FCSTD DOCUMENT  (FreeCAD 0.19R16830 +1496 (Git))
Label: asm_V4
License: All rights reserved
LicenseURL: http://en.wikipedia.org/wiki/All_rights_reserved
objects: PartDesign::CoordinateSystem×18, App::Link×13, App::FeaturePython×13, Sketcher::SketchObject×5, PartDesign::Point×4, App::DocumentObjectGroup×1, App::Part×1
note: 27 computed .brp shape members not serialized (recipe doc carries the construction recipe); baked Part::Feature solids carry a one-line shape summary decoded from their .brp
EXTERNAL_REF file=Crankshaft.FCStd obj=Model
EXTERNAL_REF file=Cylindre.FCStd obj=Part
EXTERNAL_REF file=Piston.FCStd obj=Part
EXTERNAL_REF file=asm_Bielle.fcstd obj=Model

FEATURE [PartDesign::CoordinateSystem] LCS_0
  AttacherType = Attacher::AttachEngine3D
FEATURE [PartDesign::CoordinateSystem] LCS_crankshaft
  AttacherType = Attacher::AttachEngine3D
  AttachmentOffset = pos=(0,0,0) rot=(0,1,0;12.5664rad)
  MapMode = 2
  Support = -> [LCS_0]
FEATURE [App::Link] Crankshaft
  LinkedObject = -> <external Crankshaft.FCStd>#Model
  expr: Placement = <<LCS_crankshaft>>.Placement.multiply(<<constr_Crankshaft>>.AttachmentOffset).multiply(.<<LCS_0.>>.Placement.inverse())
FEATURE [App::FeaturePython] constr_Crankshaft  # WARN: FeaturePython — macro-defined, semantics opaque (R4)
  AttachedTo = Parent Assembly
  AttachmentLCS = LCS_crankshaft
  ConstraintType = AttachmentByLCS
  LinkName = Crankshaft
  LinkedFile = Crankshaft
  LinkedPartLCS = LCS_0
FEATURE [PartDesign::Point] Point_clocking1
  AttacherType = Attacher::AttachEnginePoint
  Placement = pos=(-28.2843,6.3e-15,28.2843) rot=(0,1,0;0.785398rad)
  expr: Placement = <<Crankshaft>>.Placement.multiply(<<Crankshaft>>.<<LCS_clocking1.>>.Placement)
FEATURE [PartDesign::Point] Point_clocking2
  AttacherType = Attacher::AttachEnginePoint
  Placement = pos=(28.2843,6.3e-15,28.2843) rot=(0.382683,0,-0.92388;3.14159rad)
  expr: Placement = <<Crankshaft>>.Placement.multiply(<<Crankshaft>>.<<LCS_clocking2.>>.Placement)
FEATURE [PartDesign::Point] Point_clocking3
  AttacherType = Attacher::AttachEnginePoint
  Placement = pos=(28.2843,-6.3e-15,-28.2843) rot=(-0.382683,0,-0.92388;3.14159rad)
  expr: Placement = <<Crankshaft>>.Placement.multiply(<<Crankshaft>>.<<LCS_clocking3.>>.Placement)
FEATURE [PartDesign::Point] Point_clocking4
  AttacherType = Attacher::AttachEnginePoint
  Placement = pos=(-28.2843,-6.3e-15,-28.2843) rot=(0,-1,0;0.785398rad)
  expr: Placement = <<Crankshaft>>.Placement.multiply(<<Crankshaft>>.<<LCS_clocking4.>>.Placement)
FEATURE [PartDesign::CoordinateSystem] LCS_cylindre1
  AttacherType = Attacher::AttachEngine3D
  Placement = pos=(0,50,0) rot=(0,0,1;0rad)
  expr: Placement = <<Crankshaft>>.Placement.multiply(<<Crankshaft>>.<<LCS_cylindre1.>>.Placement)
FEATURE [PartDesign::CoordinateSystem] LCS_cylindre2
  AttacherType = Attacher::AttachEngine3D
  Placement = pos=(0,100,0) rot=(0,0,1;0rad)
  expr: Placement = <<Crankshaft>>.Placement.multiply(<<Crankshaft>>.<<LCS_cylindre2.>>.Placement)
FEATURE [PartDesign::CoordinateSystem] LCS_cylindre3
  AttacherType = Attacher::AttachEngine3D
  Placement = pos=(0,160,0) rot=(0,0,1;0rad)
  expr: Placement = <<Crankshaft>>.Placement.multiply(<<Crankshaft>>.<<LCS_cylindre3.>>.Placement)
FEATURE [PartDesign::CoordinateSystem] LCS_cylindre4
  AttacherType = Attacher::AttachEngine3D
  Placement = pos=(0,210,0) rot=(0,0,1;0rad)
  expr: Placement = <<Crankshaft>>.Placement.multiply(<<Crankshaft>>.<<LCS_cylindre4.>>.Placement)
FEATURE [Sketcher::SketchObject] Sketch_V
  MapMode = 3
  Placement = pos=(0,0,0) rot=(1,0,0;1.5708rad)
  Support = -> [LCS_0]
  sketch-geometry (2):
    g0: LineSegment StartX=0 StartY=0 StartZ=0 EndX=169.706 EndY=169.706 EndZ=0
    g1: LineSegment StartX=0 StartY=0 StartZ=0 EndX=-169.706 EndY=169.706 EndZ=0
  constraints (5):
    c: Coincident(g0,g-1)
    c: Coincident(g1,g0)
    c: Symmetric(g1,g0,g-2)
    c: Angle(g0,g1) = 1.5708
    c: Distance(g1) = 240
FEATURE [Sketcher::SketchObject] Sketch_piston1
  ExternalGeometry = -> [Sketch_V,Point_clocking1]
  MapMode = 3
  Placement = pos=(0,50,0) rot=(1,0,0;1.5708rad)
  Support = -> [LCS_cylindre1]
  sketch-geometry (4):
    g0: LineSegment StartX=0 StartY=0 StartZ=0 EndX=-28.2843 EndY=28.2843 EndZ=0
    g1: LineSegment StartX=-28.2843 StartY=28.2843 StartZ=0 EndX=-134.35 EndY=134.35 EndZ=0
    g2: LineSegment StartX=-134.35 StartY=134.35 StartZ=0 EndX=-162.635 EndY=162.635 EndZ=0
    g3: LineSegment StartX=-169.706 StartY=169.706 StartZ=0 EndX=-162.635 EndY=162.635 EndZ=0
  constraints (11):
    c: Coincident(g0,g-1)
    c: Coincident(g0,g-4)
    c: Coincident(g1,g0)
    c: PointOnObject(g1,g-3)
    c: Coincident(g2,g1)
    c: PointOnObject(g2,g-3)
    c: Parallel(g3,g-3)
    c: Coincident(g-3,g3)
    c: Distance(g3) = 10
    c: Distance(g3,g2) = 10
    c: Distance(g1) = 150
FEATURE [Sketcher::SketchObject] Sketch_piston2
  ExternalGeometry = -> [Point_clocking2,Sketch_V]
  MapMode = 3
  Placement = pos=(0,100,0) rot=(1,0,0;1.5708rad)
  Support = -> [LCS_cylindre2]
  sketch-geometry (4):
    g0: LineSegment StartX=0 StartY=0 StartZ=0 EndX=28.2843 EndY=28.2843 EndZ=0
    g1: LineSegment StartX=28.2843 StartY=28.2843 StartZ=0 EndX=134.35 EndY=134.35 EndZ=0
    g2: LineSegment StartX=134.35 StartY=134.35 StartZ=0 EndX=162.635 EndY=162.635 EndZ=0
    g3: LineSegment StartX=169.706 StartY=169.706 StartZ=0 EndX=162.635 EndY=162.635 EndZ=0
  constraints (11):
    c: Coincident(g0,g-3)
    c: Coincident(g-1,g0)
    c: Coincident(g1,g0)
    c: PointOnObject(g1,g-4)
    c: Coincident(g2,g1)
    c: PointOnObject(g2,g-4)
    c: Parallel(g3,g-4)
    c: Coincident(g3,g-4)
    c: Distance(g3) = 10
    c: Distance(g3,g2) = 10
    c: Distance(g1) = 150
FEATURE [Sketcher::SketchObject] Sketch_piston3
  ExternalGeometry = -> [Sketch_V,Point_clocking3]
  MapMode = 3
  Placement = pos=(0,160,0) rot=(1,0,0;1.5708rad)
  Support = -> [LCS_cylindre3]
  sketch-geometry (4):
    g0: LineSegment StartX=28.2843 StartY=-28.2843 StartZ=0 EndX=-1.78e-14 EndY=3.6e-15 EndZ=0
    g1: LineSegment StartX=28.2843 StartY=-28.2843 StartZ=0 EndX=-77.7817 EndY=77.7817 EndZ=0
    g2: LineSegment StartX=-169.706 StartY=169.706 StartZ=0 EndX=-162.635 EndY=162.635 EndZ=0
    g3: LineSegment StartX=-77.7817 StartY=77.7817 StartZ=0 EndX=-162.635 EndY=162.635 EndZ=0
  constraints (11):
    c: Coincident(g0,g-4)
    c: Coincident(g-1,g0)
    c: Coincident(g1,g0)
    c: PointOnObject(g1,g-3)
    c: Coincident(g2,g-3)
    c: Parallel(g2,g-3)
    c: Coincident(g3,g1)
    c: PointOnObject(g3,g-3)
    c: Distance(g2) = 10
    c: Distance(g2,g3) = 10
    c: Distance(g1) = 150
FEATURE [Sketcher::SketchObject] Sketch_piston4
  ExternalGeometry = -> [Sketch_V,Point_clocking4]
  MapMode = 3
  Placement = pos=(0,210,0) rot=(1,0,0;1.5708rad)
  Support = -> [LCS_cylindre4]
  sketch-geometry (4):
    g0: LineSegment StartX=-28.2843 StartY=-28.2843 StartZ=0 EndX=77.7817 EndY=77.7817 EndZ=0
    g1: LineSegment StartX=-28.2843 StartY=-28.2843 StartZ=0 EndX=-3.6e-15 EndY=-2.49e-14 EndZ=0
    g2: LineSegment StartX=77.7817 StartY=77.7817 StartZ=0 EndX=162.635 EndY=162.635 EndZ=0
    g3: LineSegment StartX=169.706 StartY=169.706 StartZ=0 EndX=162.635 EndY=162.635 EndZ=0
  constraints (11):
    c: Coincident(g0,g-4)
    c: PointOnObject(g0,g-3)
    c: Coincident(g1,g0)
    c: Coincident(g1,g-1)
    c: Coincident(g2,g0)
    c: PointOnObject(g2,g-3)
    c: Coincident(g3,g-3)
    c: Parallel(g3,g-3)
    c: Distance(g3) = 10
    c: Distance(g2,g3) = 10
    c: Distance(g0) = 150
FEATURE [PartDesign::CoordinateSystem] LCS_cylindre1001
  AttacherType = Attacher::AttachEngine3D
  MapMode = 50
  Placement = pos=(-169.706,50,169.706) rot=(0,1,0;0.785398rad)
  Support = -> [Sketch_piston1]
FEATURE [PartDesign::CoordinateSystem] LCS_cylindre2001
  AttacherType = Attacher::AttachEngine3D
  MapMode = 49
  Placement = pos=(169.706,100,169.706) rot=(-0.382683,0,0.92388;3.14159rad)
  Support = -> [Sketch_piston2]
FEATURE [PartDesign::CoordinateSystem] LCS_cylindre3001
  AttacherType = Attacher::AttachEngine3D
  MapMode = 49
  Placement = pos=(-169.706,160,169.706) rot=(0,1,0;0.785398rad)
  Support = -> [Sketch_piston3]
FEATURE [PartDesign::CoordinateSystem] LCS_cylindre4001
  AttacherType = Attacher::AttachEngine3D
  MapMode = 49
  Placement = pos=(169.706,210,169.706) rot=(-0.382683,0,0.92388;3.14159rad)
  Support = -> [Sketch_piston4]
FEATURE [App::Link] Cylindre_1
  LinkPlacement = pos=(-169.706,50,169.706) rot=(0,1,0;2.35619rad)
  LinkedObject = -> <external Cylindre.FCStd>#Part
  Placement = pos=(-169.706,50,169.706) rot=(0,1,0;2.35619rad)
  expr: Placement = <<LCS_cylindre1001>>.Placement.multiply(<<constr_Cylindre_1>>.AttachmentOffset).multiply(.<<LCS_0.>>.Placement.inverse())
FEATURE [App::FeaturePython] constr_Cylindre_1  # WARN: FeaturePython — macro-defined, semantics opaque (R4)
  AttachedTo = Parent Assembly
  AttachmentLCS = LCS_cylindre1001
  AttachmentOffset = pos=(0,0,0) rot=(0,1,0;1.5708rad)
  ConstraintType = AttachmentByLCS
  LinkName = Cylindre_1
  LinkedFile = Cylindre
  LinkedPartLCS = LCS_0
FEATURE [App::Link] Cylindre_2
  LinkPlacement = pos=(169.706,100,169.706) rot=(-0.92388,0,0.382683;3.14159rad)
  LinkedObject = -> <external Cylindre.FCStd>#Part
  Placement = pos=(169.706,100,169.706) rot=(-0.92388,0,0.382683;3.14159rad)
  expr: Placement = <<LCS_cylindre2001>>.Placement.multiply(<<constr_Cylindre_2>>.AttachmentOffset).multiply(.<<LCS_0.>>.Placement.inverse())
FEATURE [App::FeaturePython] constr_Cylindre_2  # WARN: FeaturePython — macro-defined, semantics opaque (R4)
  AttachedTo = Parent Assembly
  AttachmentLCS = LCS_cylindre2001
  AttachmentOffset = pos=(0,0,0) rot=(0,1,0;1.5708rad)
  ConstraintType = AttachmentByLCS
  LinkName = Cylindre_2
  LinkedFile = Cylindre
  LinkedPartLCS = LCS_0
FEATURE [App::Link] Cylindre_3
  LinkPlacement = pos=(-169.706,160,169.706) rot=(0,1,0;2.35619rad)
  LinkedObject = -> <external Cylindre.FCStd>#Part
  Placement = pos=(-169.706,160,169.706) rot=(0,1,0;2.35619rad)
  expr: Placement = <<LCS_cylindre3001>>.Placement.multiply(<<constr_Cylindre_3>>.AttachmentOffset).multiply(.<<LCS_0.>>.Placement.inverse())
FEATURE [App::FeaturePython] constr_Cylindre_3  # WARN: FeaturePython — macro-defined, semantics opaque (R4)
  AttachedTo = Parent Assembly
  AttachmentLCS = LCS_cylindre3001
  AttachmentOffset = pos=(0,0,0) rot=(0,1,0;1.5708rad)
  ConstraintType = AttachmentByLCS
  LinkName = Cylindre_3
  LinkedFile = Cylindre
  LinkedPartLCS = LCS_0
FEATURE [App::Link] Cylindre_4
  LinkPlacement = pos=(169.706,210,169.706) rot=(-0.92388,0,0.382683;3.14159rad)
  LinkedObject = -> <external Cylindre.FCStd>#Part
  Placement = pos=(169.706,210,169.706) rot=(-0.92388,0,0.382683;3.14159rad)
  expr: Placement = <<LCS_cylindre4001>>.Placement.multiply(<<constr_Cylindre_4>>.AttachmentOffset).multiply(.<<LCS_0.>>.Placement.inverse())
FEATURE [App::FeaturePython] constr_Cylindre_4  # WARN: FeaturePython — macro-defined, semantics opaque (R4)
  AttachedTo = Parent Assembly
  AttachmentLCS = LCS_cylindre4001
  AttachmentOffset = pos=(0,0,0) rot=(0,1,0;1.5708rad)
  ConstraintType = AttachmentByLCS
  LinkName = Cylindre_4
  LinkedFile = Cylindre
  LinkedPartLCS = LCS_0
FEATURE [PartDesign::CoordinateSystem] LCS_P1
  AttacherType = Attacher::AttachEngine3D
  MapMode = 49
  Placement = pos=(-134.35,50,134.35) rot=(0.382683,0,0.92388;3.14159rad)
  Support = -> [Sketch_piston1]
FEATURE [PartDesign::CoordinateSystem] LCS_B1
  AttacherType = Attacher::AttachEngine3D
  MapMode = 49
  Placement = pos=(-28.2843,50,28.2843) rot=(0.382683,0,0.92388;3.14159rad)
  Support = -> [Sketch_piston1]
FEATURE [PartDesign::CoordinateSystem] LCS_P2
  AttacherType = Attacher::AttachEngine3D
  MapMode = 49
  Placement = pos=(134.35,100,134.35) rot=(0,-1,0;0.785398rad)
  Support = -> [Sketch_piston2]
FEATURE [PartDesign::CoordinateSystem] LCS_B2
  AttacherType = Attacher::AttachEngine3D
  MapMode = 49
  Placement = pos=(28.2843,100,28.2843) rot=(0,-1,0;0.785398rad)
  Support = -> [Sketch_piston2]
FEATURE [PartDesign::CoordinateSystem] LCS_P3
  AttacherType = Attacher::AttachEngine3D
  MapMode = 49
  Placement = pos=(-77.7817,160,77.7817) rot=(0.382683,0,0.92388;3.14159rad)
  Support = -> [Sketch_piston3]
FEATURE [PartDesign::CoordinateSystem] LCS_B3
  AttacherType = Attacher::AttachEngine3D
  MapMode = 49
  Placement = pos=(28.2843,160,-28.2843) rot=(0.382683,0,0.92388;3.14159rad)
  Support = -> [Sketch_piston3]
FEATURE [PartDesign::CoordinateSystem] LCS_P4
  AttacherType = Attacher::AttachEngine3D
  MapMode = 49
  Placement = pos=(77.7817,210,77.7817) rot=(0,-1,0;0.785398rad)
  Support = -> [Sketch_piston4]
FEATURE [PartDesign::CoordinateSystem] LCS_B4
  AttacherType = Attacher::AttachEngine3D
  MapMode = 49
  Placement = pos=(-28.2843,210,-28.2843) rot=(0,-1,0;0.785398rad)
  Support = -> [Sketch_piston4]
FEATURE [App::Link] Piston_1
  LinkPlacement = pos=(-98.9949,50,98.9949) rot=(0,1,0;5.49779rad)
  LinkedObject = -> <external Piston.FCStd>#Part
  Placement = pos=(-98.9949,50,98.9949) rot=(0,1,0;5.49779rad)
  expr: Placement = <<LCS_P1>>.Placement.multiply(<<constr_Piston_1>>.AttachmentOffset).multiply(.<<LCS_axis.>>.Placement.inverse())
FEATURE [App::FeaturePython] constr_Piston_1  # WARN: FeaturePython — macro-defined, semantics opaque (R4)
  AttachedTo = Parent Assembly
  AttachmentLCS = LCS_P1
  AttachmentOffset = pos=(0,0,0) rot=(-0.57735,-0.57735,0.57735;4.18879rad)
  ConstraintType = AttachmentByLCS
  LinkName = Piston_1
  LinkedFile = Piston
  LinkedPartLCS = LCS_axis
FEATURE [App::Link] Piston_2
  LinkPlacement = pos=(98.9949,100,98.9949) rot=(-0.382683,0,-0.92388;3.14159rad)
  LinkedObject = -> <external Piston.FCStd>#Part
  Placement = pos=(98.9949,100,98.9949) rot=(-0.382683,0,-0.92388;3.14159rad)
  expr: Placement = <<LCS_P2>>.Placement.multiply(<<constr_Piston_2>>.AttachmentOffset).multiply(.<<LCS_axis.>>.Placement.inverse())
FEATURE [App::FeaturePython] constr_Piston_2  # WARN: FeaturePython — macro-defined, semantics opaque (R4)
  AttachedTo = Parent Assembly
  AttachmentLCS = LCS_P2
  AttachmentOffset = pos=(0,0,0) rot=(0.57735,0.57735,-0.57735;2.0944rad)
  ConstraintType = AttachmentByLCS
  LinkName = Piston_2
  LinkedFile = Piston
  LinkedPartLCS = LCS_axis
FEATURE [App::Link] Piston_3
  LinkPlacement = pos=(-42.4264,160,42.4264) rot=(0,1,0;5.49779rad)
  LinkedObject = -> <external Piston.FCStd>#Part
  Placement = pos=(-42.4264,160,42.4264) rot=(0,1,0;5.49779rad)
  expr: Placement = <<LCS_P3>>.Placement.multiply(<<constr_Piston_3>>.AttachmentOffset).multiply(.<<LCS_axis.>>.Placement.inverse())
FEATURE [App::FeaturePython] constr_Piston_3  # WARN: FeaturePython — macro-defined, semantics opaque (R4)
  AttachedTo = Parent Assembly
  AttachmentLCS = LCS_P3
  AttachmentOffset = pos=(0,0,0) rot=(-0.57735,-0.57735,0.57735;4.18879rad)
  ConstraintType = AttachmentByLCS
  LinkName = Piston_3
  LinkedFile = Piston
  LinkedPartLCS = LCS_axis
FEATURE [App::Link] Piston_4
  LinkPlacement = pos=(42.4264,210,42.4264) rot=(-0.382683,0,-0.92388;3.14159rad)
  LinkedObject = -> <external Piston.FCStd>#Part
  Placement = pos=(42.4264,210,42.4264) rot=(-0.382683,0,-0.92388;3.14159rad)
  expr: Placement = <<LCS_P4>>.Placement.multiply(<<constr_Piston_4>>.AttachmentOffset).multiply(.<<LCS_axis.>>.Placement.inverse())
FEATURE [App::FeaturePython] constr_Piston_4  # WARN: FeaturePython — macro-defined, semantics opaque (R4)
  AttachedTo = Parent Assembly
  AttachmentLCS = LCS_P4
  AttachmentOffset = pos=(0,0,0) rot=(0.57735,0.57735,-0.57735;2.0944rad)
  ConstraintType = AttachmentByLCS
  LinkName = Piston_4
  LinkedFile = Piston
  LinkedPartLCS = LCS_axis
FEATURE [App::Link] Bielle_1
  LinkPlacement = pos=(-116.673,50,116.673) rot=(-0.862856,0.357407,0.357407;1.71777rad)
  LinkedObject = -> <external asm_Bielle.fcstd>#Model
  Placement = pos=(-116.673,50,116.673) rot=(-0.862856,0.357407,0.357407;1.71777rad)
  expr: Placement = <<LCS_B1>>.Placement.multiply(<<constr_Bielle_1>>.AttachmentOffset).multiply(.<<LCS_Cuve.>>.Placement.inverse())
FEATURE [App::FeaturePython] constr_Bielle_1  # WARN: FeaturePython — macro-defined, semantics opaque (R4)
  AttachedTo = Parent Assembly
  AttachmentLCS = LCS_B1
  AttachmentOffset = pos=(0,0,0) rot=(0,0.707107,-0.707107;3.14159rad)
  ConstraintType = AttachmentByLCS
  LinkName = Bielle_1
  LinkedFile = asm_Bielle
  LinkedPartLCS = LCS_Cuve
FEATURE [App::Link] Bielle_2
  LinkPlacement = pos=(116.673,100,116.673) rot=(-0.281085,-0.678598,0.678598;3.68962rad)
  LinkedObject = -> <external asm_Bielle.fcstd>#Model
  Placement = pos=(116.673,100,116.673) rot=(-0.281085,-0.678598,0.678598;3.68962rad)
  expr: Placement = <<LCS_B2>>.Placement.multiply(<<constr_Bielle_2>>.AttachmentOffset).multiply(.<<LCS_Cuve.>>.Placement.inverse())
FEATURE [App::FeaturePython] constr_Bielle_2  # WARN: FeaturePython — macro-defined, semantics opaque (R4)
  AttachedTo = Parent Assembly
  AttachmentLCS = LCS_B2
  AttachmentOffset = pos=(0,0,0) rot=(0,-0.707107,0.707107;3.14159rad)
  ConstraintType = AttachmentByLCS
  LinkName = Bielle_2
  LinkedFile = asm_Bielle
  LinkedPartLCS = LCS_Cuve
FEATURE [App::Link] Bielle_3
  LinkPlacement = pos=(-60.1041,160,60.1041) rot=(0.862856,-0.357407,-0.357407;4.56541rad)
  LinkedObject = -> <external asm_Bielle.fcstd>#Model
  Placement = pos=(-60.1041,160,60.1041) rot=(0.862856,-0.357407,-0.357407;4.56541rad)
  expr: Placement = <<LCS_B3>>.Placement.multiply(<<constr_Bielle_3>>.AttachmentOffset).multiply(.<<LCS_Cuve.>>.Placement.inverse())
FEATURE [App::FeaturePython] constr_Bielle_3  # WARN: FeaturePython — macro-defined, semantics opaque (R4)
  AttachedTo = Parent Assembly
  AttachmentLCS = LCS_B3
  AttachmentOffset = pos=(0,0,0) rot=(0,-0.707107,0.707107;3.14159rad)
  ConstraintType = AttachmentByLCS
  LinkName = Bielle_3
  LinkedFile = asm_Bielle
  LinkedPartLCS = LCS_Cuve
FEATURE [App::Link] Bielle_4
  LinkPlacement = pos=(60.1041,210,60.1041) rot=(0.281085,0.678598,-0.678598;2.59356rad)
  LinkedObject = -> <external asm_Bielle.fcstd>#Model
  Placement = pos=(60.1041,210,60.1041) rot=(0.281085,0.678598,-0.678598;2.59356rad)
  expr: Placement = <<LCS_B4>>.Placement.multiply(<<constr_Bielle_4>>.AttachmentOffset).multiply(.<<LCS_Cuve.>>.Placement.inverse())
FEATURE [App::FeaturePython] constr_Bielle_4  # WARN: FeaturePython — macro-defined, semantics opaque (R4)
  AttachedTo = Parent Assembly
  AttachmentLCS = LCS_B4
  AttachmentOffset = pos=(0,0,0) rot=(0,0.707107,-0.707107;3.14159rad)
  ConstraintType = AttachmentByLCS
  LinkName = Bielle_4
  LinkedFile = asm_Bielle
  LinkedPartLCS = LCS_Cuve
FEATURE [App::DocumentObjectGroup] Constraints
  Group = -> [constr_Crankshaft,constr_Cylindre_1,constr_Cylindre_2,constr_Cylindre_3,constr_Cylindre_4,constr_Piston_1,constr_Piston_2,constr_Piston_3,constr_Piston_4,constr_Bielle_1,constr_Bielle_2,constr_Bielle_3,constr_Bielle_4]
FEATURE [App::Part] Model
  Group = -> [Constraints,LCS_0,LCS_crankshaft,Crankshaft,constr_Crankshaft,Point_clocking1,Point_clocking2,Point_clocking3,Point_clocking4,LCS_cylindre1,LCS_cylindre2,LCS_cylindre3,LCS_cylindre4,Sketch_V,Sketch_piston1,Sketch_piston2,Sketch_piston3,Sketch_piston4,LCS_cylindre1001,LCS_cylindre2001,LCS_cylindre3001,LCS_cylindre4001,Cylindre_1,constr_Cylindre_1,Cylindre_2,constr_Cylindre_2,Cylindre_3,+27 more]
  Origin = -> Origin

RESOLVED EXTERNAL PARTS (link-assembly join: the EXTERNAL_REF files above that resolve inside this repo's crawl, each included once):
---- part Crankshaft.FCStd = doc fcstd_91660418393e ----
FCSTD DOCUMENT  (FreeCAD 0.18R16268 (Git))
Label: Crankshaft
License: All rights reserved
LicenseURL: http://en.wikipedia.org/wiki/All_rights_reserved
objects: Sketcher::SketchObject×11, PartDesign::CoordinateSystem×9, App::DocumentObjectGroup×1, App::Part×1
note: 20 computed .brp shape members not serialized (recipe doc carries the construction recipe); baked Part::Feature solids carry a one-line shape summary decoded from their .brp

FEATURE [App::DocumentObjectGroup] Constraints
FEATURE [PartDesign::CoordinateSystem] LCS_0
  AttacherType = Attacher::AttachEngine3D
FEATURE [Sketcher::SketchObject] Sketch_arrow
  MapMode = 3
  Placement = pos=(0,0,0) rot=(1,0,0;1.5708rad)
  Support = -> [LCS_0]
  sketch-geometry (3):
    g0: LineSegment StartX=0 StartY=0 StartZ=0 EndX=0 EndY=75 EndZ=0
    g1: LineSegment StartX=0 StartY=75 StartZ=0 EndX=7.5 EndY=62.0096 EndZ=0
    g2: LineSegment StartX=0 StartY=75 StartZ=0 EndX=-7.5 EndY=62.0096 EndZ=0
  constraints (8):
    c: Coincident(g0,g-1)
    c: Vertical(g0)
    c: Coincident(g1,g0)
    c: Coincident(g2,g0)
    c: Symmetric(g2,g1,g-2)
    c: Angle(g2,g1) = 1.0472
    c: DistanceY(g0,g0) = 75
    c: Distance(g1) = 15
FEATURE [Sketcher::SketchObject] Sketch_pos_cylindres
  MapMode = 4
  Placement = pos=(0,0,0) rot=(0.57735,0.57735,0.57735;2.0944rad)
  Support = -> [LCS_0]
  sketch-geometry (5):
    g0: LineSegment StartX=0 StartY=0 StartZ=0 EndX=50 EndY=0 EndZ=0
    g1: LineSegment StartX=50 StartY=0 StartZ=0 EndX=100 EndY=0 EndZ=0
    g2: LineSegment StartX=100 StartY=0 StartZ=0 EndX=160 EndY=0 EndZ=0
    g3: LineSegment StartX=160 StartY=0 StartZ=0 EndX=210 EndY=0 EndZ=0
    g4: LineSegment StartX=210 StartY=0 StartZ=0 EndX=260 EndY=0 EndZ=0
  constraints (15):
    c: Coincident(g0,g-1)
    c: PointOnObject(g0,g-1)
    c: Coincident(g1,g0)
    c: Horizontal(g1)
    c: Coincident(g2,g1)
    c: Horizontal(g2)
    c: Coincident(g3,g2)
    c: Horizontal(g3)
    c: Coincident(g4,g3)
    c: Horizontal(g4)
    c: DistanceX(g4,g4) = 50
    c: DistanceX(g2,g2) = 60
    c: DistanceX(g1,g1) = 50
    c: DistanceX(g0,g0) = 50
    c: Equal(g1,g3)
FEATURE [Sketcher::SketchObject] Sketch_travel
  MapMode = 3
  Placement = pos=(0,0,0) rot=(1,0,0;1.5708rad)
  Support = -> [LCS_0]
  sketch-geometry (1):
    g0: Circle CenterX=0 CenterY=0 CenterZ=0 NormalX=0 NormalY=0 NormalZ=1 AngleXU=0 Radius=40
  constraints (2):
    c: Coincident(g0,g-1)
    c: Diameter(g0) = 80
FEATURE [Sketcher::SketchObject] Sketch_clocking1
  ExternalGeometry = -> [Sketch_travel]
  MapMode = 3
  Placement = pos=(0,0,0) rot=(1,0,0;1.5708rad)
  Support = -> [LCS_0]
  sketch-geometry (1):
    g0: LineSegment StartX=0 StartY=0 StartZ=0 EndX=-28.2843 EndY=28.2843 EndZ=0
  constraints (3):
    c: Coincident(g0,g-1)
    c: PointOnObject(g0,g-3)
    c: Angle(g-2,g0) = 0.785398
FEATURE [Sketcher::SketchObject] Sketch_clocking2
  ExternalGeometry = -> [Sketch_travel]
  MapMode = 3
  Placement = pos=(0,0,0) rot=(1,0,0;1.5708rad)
  Support = -> [LCS_0]
  sketch-geometry (1):
    g0: LineSegment StartX=0 StartY=0 StartZ=0 EndX=28.2843 EndY=28.2843 EndZ=0
  constraints (3):
    c: Coincident(g0,g-1)
    c: PointOnObject(g0,g-3)
    c: Angle(g-2,g0) = -0.785398
FEATURE [Sketcher::SketchObject] Sketch_clocking3
  ExternalGeometry = -> [Sketch_travel]
  MapMode = 3
  Placement = pos=(0,0,0) rot=(1,0,0;1.5708rad)
  Support = -> [LCS_0]
  sketch-geometry (1):
    g0: LineSegment StartX=0 StartY=0 StartZ=0 EndX=28.2843 EndY=-28.2843 EndZ=0
  constraints (3):
    c: Coincident(g0,g-1)
    c: PointOnObject(g0,g-3)
    c: Angle(g-2,g0) = 3.92699
FEATURE [Sketcher::SketchObject] Sketch_clocking4
  ExternalGeometry = -> [Sketch_travel]
  MapMode = 3
  Placement = pos=(0,0,0) rot=(1,0,0;1.5708rad)
  Support = -> [LCS_0]
  sketch-geometry (1):
    g0: LineSegment StartX=0 StartY=0 StartZ=0 EndX=-28.2843 EndY=-28.2843 EndZ=0
  constraints (3):
    c: Coincident(g0,g-1)
    c: PointOnObject(g0,g-3)
    c: Angle(g-2,g0) = 2.35619
FEATURE [PartDesign::CoordinateSystem] LCS_clocking1
  AttacherType = Attacher::AttachEngine3D
  AttachmentOffset = pos=(0,0,0) rot=(1,0,0;3.14159rad)
  MapMode = 49
  Placement = pos=(-28.2843,6.3e-15,28.2843) rot=(0,1,0;0.785398rad)
  Support = -> [Sketch_clocking1]
FEATURE [PartDesign::CoordinateSystem] LCS_clocking2
  AttacherType = Attacher::AttachEngine3D
  AttachmentOffset = pos=(0,0,0) rot=(1,0,0;3.14159rad)
  MapMode = 49
  Placement = pos=(28.2843,6.3e-15,28.2843) rot=(0.382683,0,-0.92388;3.14159rad)
  Support = -> [Sketch_clocking2]
FEATURE [PartDesign::CoordinateSystem] LCS_clocking3
  AttacherType = Attacher::AttachEngine3D
  AttachmentOffset = pos=(0,0,0) rot=(1,0,0;3.14159rad)
  MapMode = 49
  Placement = pos=(28.2843,-6.3e-15,-28.2843) rot=(-0.382683,0,-0.92388;3.14159rad)
  Support = -> [Sketch_clocking3]
FEATURE [PartDesign::CoordinateSystem] LCS_clocking4
  AttacherType = Attacher::AttachEngine3D
  AttachmentOffset = pos=(0,0,0) rot=(1,0,0;3.14159rad)
  MapMode = 49
  Placement = pos=(-28.2843,-6.3e-15,-28.2843) rot=(0,-1,0;0.785398rad)
  Support = -> [Sketch_clocking4]
FEATURE [PartDesign::CoordinateSystem] LCS_cylindre1
  AttacherType = Attacher::AttachEngine3D
  MapMode = 1
  Placement = pos=(0,50,0) rot=(0,0,1;0rad)
  Support = -> [Sketch_pos_cylindres]
FEATURE [PartDesign::CoordinateSystem] LCS_cylindre2
  AttacherType = Attacher::AttachEngine3D
  MapMode = 1
  Placement = pos=(0,100,0) rot=(0,0,1;0rad)
  Support = -> [Sketch_pos_cylindres]
FEATURE [PartDesign::CoordinateSystem] LCS_cylindre3
  AttacherType = Attacher::AttachEngine3D
  MapMode = 1
  Placement = pos=(0,160,0) rot=(0,0,1;0rad)
  Support = -> [Sketch_pos_cylindres]
FEATURE [PartDesign::CoordinateSystem] LCS_cylindre4
  AttacherType = Attacher::AttachEngine3D
  MapMode = 1
  Placement = pos=(0,210,0) rot=(0,0,1;0rad)
  Support = -> [Sketch_pos_cylindres]
FEATURE [Sketcher::SketchObject] Sketch_1
  ExternalGeometry = -> [Sketch_clocking1]
  MapMode = 3
  Placement = pos=(0,50,0) rot=(1,0,0;1.5708rad)
  Support = -> [LCS_cylindre1]
  sketch-geometry (1):
    g0: Circle CenterX=-28.2843 CenterY=28.2843 CenterZ=0 NormalX=0 NormalY=0 NormalZ=1 AngleXU=0 Radius=15
  constraints (2):
    c: Coincident(g0,g-3)
    c: Diameter(g0) = 30
FEATURE [Sketcher::SketchObject] Sketch_2
  ExternalGeometry = -> [Sketch_clocking2]
  MapMode = 3
  Placement = pos=(0,100,0) rot=(1,0,0;1.5708rad)
  Support = -> [LCS_cylindre2]
  sketch-geometry (1):
    g0: Circle CenterX=28.2843 CenterY=28.2843 CenterZ=0 NormalX=0 NormalY=0 NormalZ=1 AngleXU=0 Radius=15
  constraints (2):
    c: Coincident(g0,g-3)
    c: Diameter(g0) = 30
FEATURE [Sketcher::SketchObject] Sketch_3
  ExternalGeometry = -> [Sketch_clocking3]
  MapMode = 3
  Placement = pos=(0,160,0) rot=(1,0,0;1.5708rad)
  Support = -> [LCS_cylindre3]
  sketch-geometry (1):
    g0: Circle CenterX=28.2843 CenterY=-28.2843 CenterZ=0 NormalX=0 NormalY=0 NormalZ=1 AngleXU=0 Radius=15
  constraints (2):
    c: Coincident(g0,g-3)
    c: Diameter(g0) = 30
FEATURE [Sketcher::SketchObject] Sketch_4
  ExternalGeometry = -> [Sketch_clocking4]
  MapMode = 3
  Placement = pos=(0,210,0) rot=(1,0,0;1.5708rad)
  Support = -> [LCS_cylindre4]
  sketch-geometry (1):
    g0: Circle CenterX=-28.2843 CenterY=-28.2843 CenterZ=0 NormalX=0 NormalY=0 NormalZ=1 AngleXU=0 Radius=15
  constraints (2):
    c: Coincident(g0,g-3)
    c: Diameter(g0) = 30
FEATURE [App::Part] Model
  Group = -> [Constraints,LCS_0,Sketch_arrow,Sketch_pos_cylindres,Sketch_travel,Sketch_clocking1,Sketch_clocking2,Sketch_clocking3,Sketch_clocking4,LCS_clocking1,LCS_clocking2,LCS_clocking3,LCS_clocking4,LCS_cylindre1,LCS_cylindre2,LCS_cylindre3,LCS_cylindre4,Sketch_1,Sketch_2,Sketch_3,Sketch_4]
  Origin = -> Origin
---- part Cylindre.FCStd = doc fcstd_e18bdc0a72f6 ----
FCSTD DOCUMENT  (FreeCAD 0.18R16268 (Git))
Label: Cylindre
License: All rights reserved
LicenseURL: http://en.wikipedia.org/wiki/All_rights_reserved
objects: PartDesign::CoordinateSystem×2, App::DocumentObjectGroup×1, PartDesign::Plane×1, Sketcher::SketchObject×1, PartDesign::Pad×1, PartDesign::Body×1, App::Part×1
note: 7 computed .brp shape members not serialized (recipe doc carries the construction recipe); baked Part::Feature solids carry a one-line shape summary decoded from their .brp

FEATURE [App::DocumentObjectGroup] Constraints
FEATURE [PartDesign::CoordinateSystem] LCS
  AttacherType = Attacher::AttachEngine3D
  MapMode = 2
FEATURE [PartDesign::Plane] DatumPlane  label="Plan_XY"
  Length = 120
  MapMode = 2
  ResizeMode = 0
  Support = -> [LCS]
  Width = 120
FEATURE [Sketcher::SketchObject] Sketch
  MapMode = 5
  Support = -> [DatumPlane]
  sketch-geometry (4):
    g0: Circle CenterX=0 CenterY=-1e-16 CenterZ=0 NormalX=0 NormalY=0 NormalZ=1 AngleXU=0 Radius=45
    g1: Circle CenterX=0 CenterY=-1e-16 CenterZ=0 NormalX=0 NormalY=0 NormalZ=1 AngleXU=0 Radius=50
    g2: GeomPoint X=0 Y=45 Z=0
    g3: GeomPoint X=0 Y=50 Z=0
  constraints (8):
    c: Coincident(g0,g-1)
    c: Coincident(g1,g0)
    c: Diameter(g0) = 90
    c: PointOnObject(g2,g0)
    c: PointOnObject(g3,g1)
    c: PointOnObject(g3,g-2)
    c: PointOnObject(g2,g-2)
    c: DistanceY(g2,g3) = 5
FEATURE [PartDesign::Pad] Pad
  ClaimChildren = false
  Length = 175
  Length2 = 100
  Profile = -> Sketch
  Type = 0
FEATURE [PartDesign::Body] Body
  Group = -> [LCS,DatumPlane,Sketch,Pad]
  Origin = -> Origin001
  Tip = -> Pad
FEATURE [PartDesign::CoordinateSystem] LCS_0
  AttacherType = Attacher::AttachEngine3D
FEATURE [App::Part] Part
  Group = -> [Constraints,Body,LCS_0]
  Origin = -> Origin
---- part asm_Bielle.fcstd = doc fcstd_c2605bcfada9 ----
FCSTD DOCUMENT  (FreeCAD 0.18R16268 (Git))
Label: asm_Bielle
License: All rights reserved
LicenseURL: http://en.wikipedia.org/wiki/All_rights_reserved
objects: App::Link×5, App::FeaturePython×5, PartDesign::CoordinateSystem×2, App::DocumentObjectGroup×1, App::Part×1
note: 2 computed .brp shape members not serialized (recipe doc carries the construction recipe); baked Part::Feature solids carry a one-line shape summary decoded from their .brp
EXTERNAL_REF file=Bielle.fcstd obj=Model
EXTERNAL_REF file=Cuve.fcstd obj=Model
EXTERNAL_REF file=Bague.fcstd obj=Model
EXTERNAL_REF file=Screw_CHC.fcstd obj=Model

FEATURE [PartDesign::CoordinateSystem] LCS_0
  AttacherType = Attacher::AttachEngine3D
FEATURE [App::Link] Bielle
  LinkedObject = -> <external Bielle.fcstd>#Model
  expr: Placement = <<LCS_0>>.Placement.multiply(<<constr_Bielle>>.AttachmentOffset).multiply(.<<LCS_0.>>.Placement.inverse())
FEATURE [App::FeaturePython] constr_Bielle  # WARN: FeaturePython — macro-defined, semantics opaque (R4)
  AttachedTo = Parent Assembly
  AttachmentLCS = LCS_0
  Link_Name = Bielle
  LinkedPartLCS = LCS_0
  Linked_File = Bielle
FEATURE [App::Link] Cuve
  LinkPlacement = pos=(125,0,0) rot=(0,0,1;0rad)
  LinkedObject = -> <external Cuve.fcstd>#Model
  Placement = pos=(125,0,0) rot=(0,0,1;0rad)
  expr: Placement = <<Bielle>>.Placement.multiply(<<Bielle>>.<<LCS_1.>>.Placement).multiply(<<constr_Cuve>>.AttachmentOffset).multiply(.<<LCS_0.>>.Placement.inverse())
FEATURE [App::FeaturePython] constr_Cuve  # WARN: FeaturePython — macro-defined, semantics opaque (R4)
  AttachedTo = Bielle
  AttachmentLCS = LCS_1
  Link_Name = Cuve
  LinkedPartLCS = LCS_0
  Linked_File = Cuve
FEATURE [App::Link] Bague
  LinkPlacement = pos=(0,0,-15) rot=(0,0,1;0rad)
  LinkedObject = -> <external Bague.fcstd>#Model
  Placement = pos=(0,0,-15) rot=(0,0,1;0rad)
  expr: Placement = <<Bielle>>.Placement.multiply(<<Bielle>>.<<LCS_0.>>.Placement).multiply(<<constr_Bague>>.AttachmentOffset).multiply(.<<LCS_0.>>.Placement.inverse())
FEATURE [App::FeaturePython] constr_Bague  # WARN: FeaturePython — macro-defined, semantics opaque (R4)
  AttachedTo = Bielle
  AttachmentLCS = LCS_0
  AttachmentOffset = pos=(0,0,-15) rot=(0,0,1;0rad)
  Link_Name = Bague
  LinkedPartLCS = LCS_0
  Linked_File = Bague
FEATURE [App::Link] Screw_CHC_1
  LinkPlacement = pos=(130,-32.5,-1.7e-14) rot=(0.707107,0,0.707107;3.14159rad)
  LinkedObject = -> <external Screw_CHC.fcstd>#Model
  Placement = pos=(130,-32.5,-1.7e-14) rot=(0.707107,0,0.707107;3.14159rad)
  expr: Placement = <<Cuve>>.Placement.multiply(<<Cuve>>.<<LCS_1.>>.Placement).multiply(<<constr_Screw_CHC_1>>.AttachmentOffset).multiply(.<<LCS_0.>>.Placement.inverse())
FEATURE [App::FeaturePython] constr_Screw_CHC_1  # WARN: FeaturePython — macro-defined, semantics opaque (R4)
  AttachedTo = Cuve
  AttachmentLCS = LCS_1
  Link_Name = Screw_CHC_1
  LinkedPartLCS = LCS_0
  Linked_File = Screw_CHC
FEATURE [App::Link] Screw_CHC_2
  LinkPlacement = pos=(130,32.5,-2.6e-15) rot=(0.707107,0,0.707107;3.14159rad)
  LinkedObject = -> <external Screw_CHC.fcstd>#Model
  Placement = pos=(130,32.5,-2.6e-15) rot=(0.707107,0,0.707107;3.14159rad)
  expr: Placement = <<Cuve>>.Placement.multiply(<<Cuve>>.<<LCS_2.>>.Placement).multiply(<<constr_Screw_CHC_2>>.AttachmentOffset).multiply(.<<LCS_0.>>.Placement.inverse())
FEATURE [App::FeaturePython] constr_Screw_CHC_2  # WARN: FeaturePython — macro-defined, semantics opaque (R4)
  AttachedTo = Cuve
  AttachmentLCS = LCS_2
  Link_Name = Screw_CHC_2
  LinkedPartLCS = LCS_0
  Linked_File = Screw_CHC
FEATURE [App::DocumentObjectGroup] Constraints
  Group = -> [constr_Bielle,constr_Cuve,constr_Bague,constr_Screw_CHC_1,constr_Screw_CHC_2]
FEATURE [PartDesign::CoordinateSystem] LCS_Cuve
  AttacherType = Attacher::AttachEngine3D
  Placement = pos=(125,0,0) rot=(0,0,1;0rad)
  expr: Placement = <<Cuve>>.Placement.multiply(<<Cuve>>.<<LCS_0.>>.Placement)
FEATURE [App::Part] Model
  Group = -> [Constraints,LCS_0,Bielle,constr_Bielle,Cuve,constr_Cuve,Bague,constr_Bague,Screw_CHC_1,constr_Screw_CHC_1,Screw_CHC_2,constr_Screw_CHC_2,LCS_Cuve]
  Origin = -> Origin
